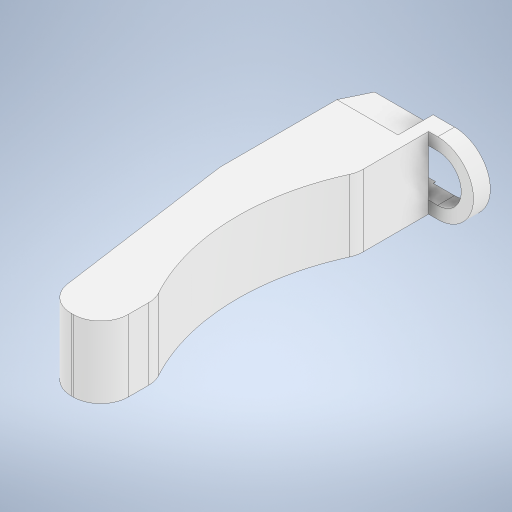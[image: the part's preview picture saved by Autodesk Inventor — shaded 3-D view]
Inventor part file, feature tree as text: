
AUTODESK INVENTOR PART (.ipt)
format: ipt  version: 2024 (Build 280153000, 153)  size: 560,128 bytes
history: native  units: in
note: dims shown in document units (in); Inventor stores cm internally (conversion verified against a paired STEP export)
features: extrude x4, sketch x2, other x1, plane x1, mirror x1, shell x1, projected_geometry x1, fillet x1
ambient origin geometry x8: Origin, YZ Plane, XZ Plane, XY Plane, X Axis, Y Axis, Z Axis, Center Point
bodies: Solid1 (feature_tree)
feature tree (12):
  other  "Plane1"
  sketch  "Sketch1"  dims[d10=0.0787in d11=0.0787in]
  extrude  "Extrusion1"  Depth=0.0787in
  extrude  "Extrusion2"  Depth=0.0787in
  plane  "Work Plane2"
  extrude  "Extrusion3"  TaperAngle=0.0deg  [1 undecoded]
  extrude  "Extrusion4"  TaperAngle=0.0deg  [1 undecoded]
  mirror  "Mirror1"
  shell  "Shell1"  Thickness=0.035in
  projected_geometry  "Projected Loop1"
  sketch  "Sketch2"  dims[d12=45.0deg d13=0.0414in d14=0.0in d15=0.0in d16=0.035in d17=0.0461in d18=0.0242in d19=0.0108in d20=0.035in d21=0.1969in d22=0.1969in d23=0.0134in d24=0.0423in d25=0.0in d26=0.0in d27=0.3937in d28=0.0in d29=0.0846in d30=0.0846in d31=0.3937in d32=0.0in d33=0.0394in d34=0.0394in d35=0.0in d36=0.0in d37=0.0787in]
  fillet  "Fillet1"  Radius=0.0461in
note: 2 required parameter values undecoded (feature->parameter linkage not recoverable at this tier; creation-order binding heuristic only, values carry confidence <= 0.55)
